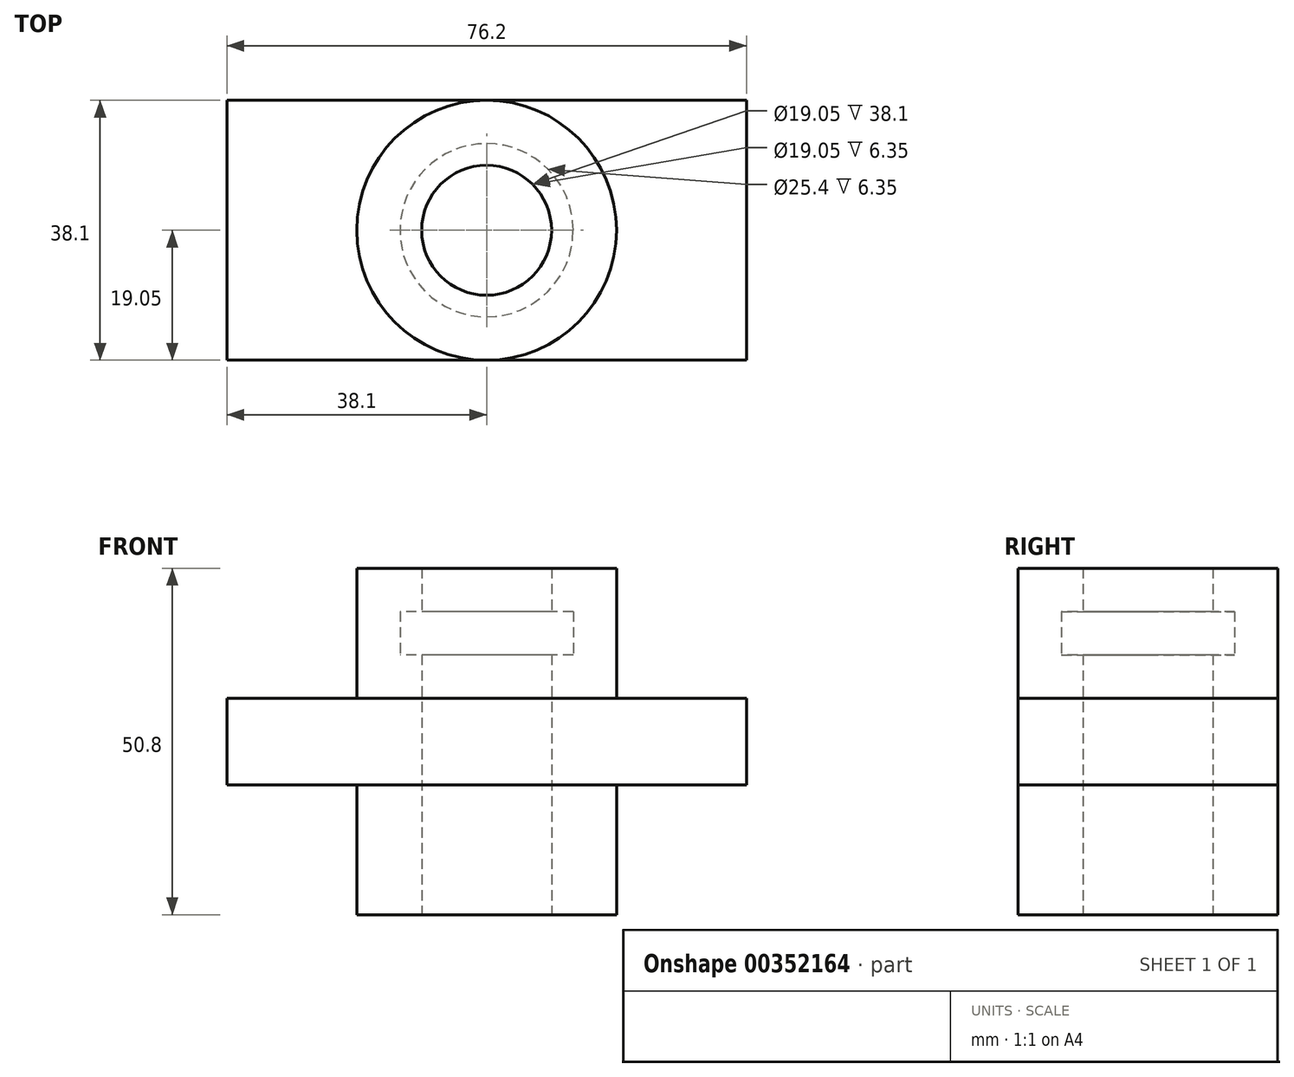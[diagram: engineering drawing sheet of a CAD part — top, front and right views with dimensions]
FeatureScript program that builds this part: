
annotation { "Feature Type Name" : "Feature", "Feature Type Description" : "" }
export const myFeature = defineFeature(function(context is Context, id is Id, definition is map)
    precondition{}
    {
        {
            var Q0;
            Q0=qCreatedBy(makeId("Top.planeOp"),FACE);
            var sketch = newSketch(context, id + "F0", { "sketchPlane" : qUnion([Q0])});
            skLineSegment(sketch, "E0.bottom", {"start": v(0, 0) * mm, "end": v(76.2, 0) * mm});
            skLineSegment(sketch, "E0.top", {"start": v(0, 38.1) * mm, "end": v(76.2, 38.1) * mm});
            skLineSegment(sketch, "E0.left", {"start": v(0, 0) * mm, "end": v(0, 38.1) * mm});
            skLineSegment(sketch, "E0.right", {"start": v(76.2, 0) * mm, "end": v(76.2, 38.1) * mm});
            skCircle(sketch, "E1", {"center": v(38.1, 19.05) * mm, "radius": 19.05 * mm});
            skCircle(sketch, "E2", {"center": v(38.1, 19.05) * mm, "radius": 9.53 * mm});
            skPoint(sketch, "E3", {"position": v(0, 19.05) * mm});
            skPoint(sketch, "E4", {"position": v(38.1, 0) * mm});
            skSolve(sketch);
        }
        {
            var Q0;
            {var subQ0=sQuery(id+"F0.wireOp",EDGE,"E0.left");Q0=makeQuery(id+"F0.imprint","IMPRINT",FACE,{"disambiguationData":[TD([[makeQuery(id+"F0.imprint","IMPRINT",EDGE,{"derivedFrom":subQ0}),-1.0]])]});}
            var Q1;
            {var subQ0=sQuery(id+"F0.wireOp",EDGE,"E0.right");Q1=makeQuery(id+"F0.imprint","IMPRINT",FACE,{"disambiguationData":[TD([[makeQuery(id+"F0.imprint","IMPRINT",EDGE,{"derivedFrom":subQ0}),1.0]])]});}
            var Q2;
            Q2=makeQuery(id+"F0.imprint","IMPRINT",FACE,{"disambiguationData":[TD([[makeQuery(id+"F0.imprint","IMPRINT",EDGE,{"derivedFrom":sQuery(id+"F0.wireOp",EDGE,"E2")}),-1.0]])]});
            extrude(context, id + "F1", {"entities" : qUnion([Q0, Q1, Q2]), "depth" : 12.7 * mm});
        }
        {
            var Q0;
            Q0=makeQuery(id+"F0.imprint","IMPRINT",FACE,{"disambiguationData":[TD([[makeQuery(id+"F0.imprint","IMPRINT",EDGE,{"derivedFrom":sQuery(id+"F0.wireOp",EDGE,"E2")}),-1.0]])]});
            extrude(context, id + "F2", {"entities" : qUnion([Q0]), "operationType" : NewBodyOperationType.ADD, "depth" : 19.05 * mm});
        }
        {
            var Q0;
            Q0=makeQuery(id+"F0.imprint","IMPRINT",FACE,{"disambiguationData":[TD([[makeQuery(id+"F0.imprint","IMPRINT",EDGE,{"derivedFrom":sQuery(id+"F0.wireOp",EDGE,"E2")}),-1.0]])]});
            extrude(context, id + "F3", {"entities" : qUnion([Q0]), "operationType" : NewBodyOperationType.ADD, "oppositeDirection" : true, "depth" : 19.05 * mm});
        }
        {
            var Q0;
            Q0=makeQuery(id+"F2.opExtrude","CAP_FACE",FACE,{"disambiguationData":[OSD([sQuery(id+"F0.wireOp",EDGE,"E1"),sQuery(id+"F0.wireOp",EDGE,"E2")])],"isStart":false});
            var sketch = newSketch(context, id + "F4", { "sketchPlane" : qUnion([Q0])});
            skCircle(sketch, "E5", {"center": v(38.1, 19.05) * mm, "radius": 12.7 * mm});
            skSolve(sketch);
        }
        {
            var Q0;
            Q0=makeQuery(id+"F2.opExtrude","CAP_FACE",FACE,{"disambiguationData":[OSD([sQuery(id+"F0.wireOp",EDGE,"E1"),sQuery(id+"F0.wireOp",EDGE,"E2")])],"isStart":false});
            extrude(context, id + "F5", {"entities" : qUnion([Q0]), "operationType" : NewBodyOperationType.ADD, "depth" : 12.7 * mm});
        }
        {
            var Q0;
            Q0 = qSketchRegion(id + "F4", true);
            extrude(context, id + "F6", {"entities" : qUnion([Q0]), "operationType" : NewBodyOperationType.REMOVE, "depth" : 6.35 * mm});
        }
    });
